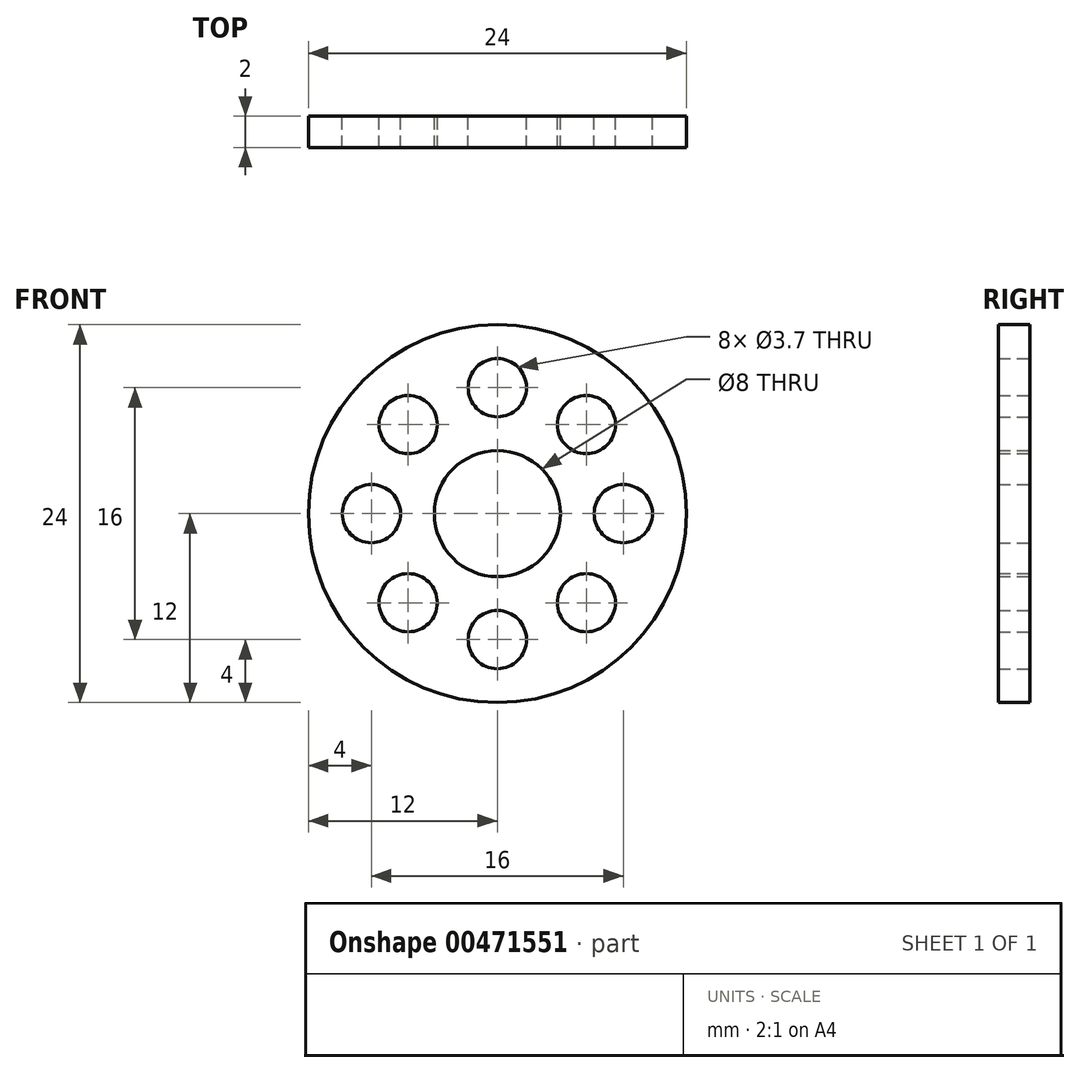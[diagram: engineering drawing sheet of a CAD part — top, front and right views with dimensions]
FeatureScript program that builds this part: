
annotation { "Feature Type Name" : "Feature", "Feature Type Description" : "" }
export const myFeature = defineFeature(function(context is Context, id is Id, definition is map)
    precondition{}
    {
        {
            var Q0;
            Q0=qCreatedBy(makeId("Front.planeOp"),FACE);
            var sketch = newSketch(context, id + "F0", { "sketchPlane" : qUnion([Q0])});
            skCircle(sketch, "E0", {"center": v(0, 0) * mm, "radius": 12 * mm});
            skCircle(sketch, "E1", {"center": v(0, 0) * mm, "radius": 4 * mm});
            skCircle(sketch, "E2", {"center": v(0, 8) * mm, "radius": 1.85 * mm});
            skCircle(sketch, "E3.1.0", {"center": v(-5.66, 5.66) * mm, "radius": 1.85 * mm});
            skCircle(sketch, "E3.2.0", {"center": v(-8, 0) * mm, "radius": 1.85 * mm});
            skCircle(sketch, "E3.3.0", {"center": v(-5.66, -5.66) * mm, "radius": 1.85 * mm});
            skCircle(sketch, "E3.4.0", {"center": v(0, -8) * mm, "radius": 1.85 * mm});
            skCircle(sketch, "E3.5.0", {"center": v(5.66, -5.66) * mm, "radius": 1.85 * mm});
            skCircle(sketch, "E3.6.0", {"center": v(8, 0) * mm, "radius": 1.85 * mm});
            skCircle(sketch, "E3.7.0", {"center": v(5.66, 5.66) * mm, "radius": 1.85 * mm});
            skLineSegment(sketch, "E4", {"start": v(0, 8) * mm, "end": v(0, 12) * mm});
            skLineSegment(sketch, "E5", {"start": v(0, 8) * mm, "end": v(0, 0) * mm});
            skSolve(sketch);
        }
        {
            var Q0;
            Q0=makeQuery(id+"F0.imprint","IMPRINT",FACE,{"disambiguationData":[TD([[makeQuery(id+"F0.imprint","IMPRINT",EDGE,{"derivedFrom":sQuery(id+"F0.wireOp",EDGE,"E0")}),1.0]])]});
            extrude(context, id + "F1", {"entities" : qUnion([Q0]), "depth" : 2 * mm});
        }
    });
